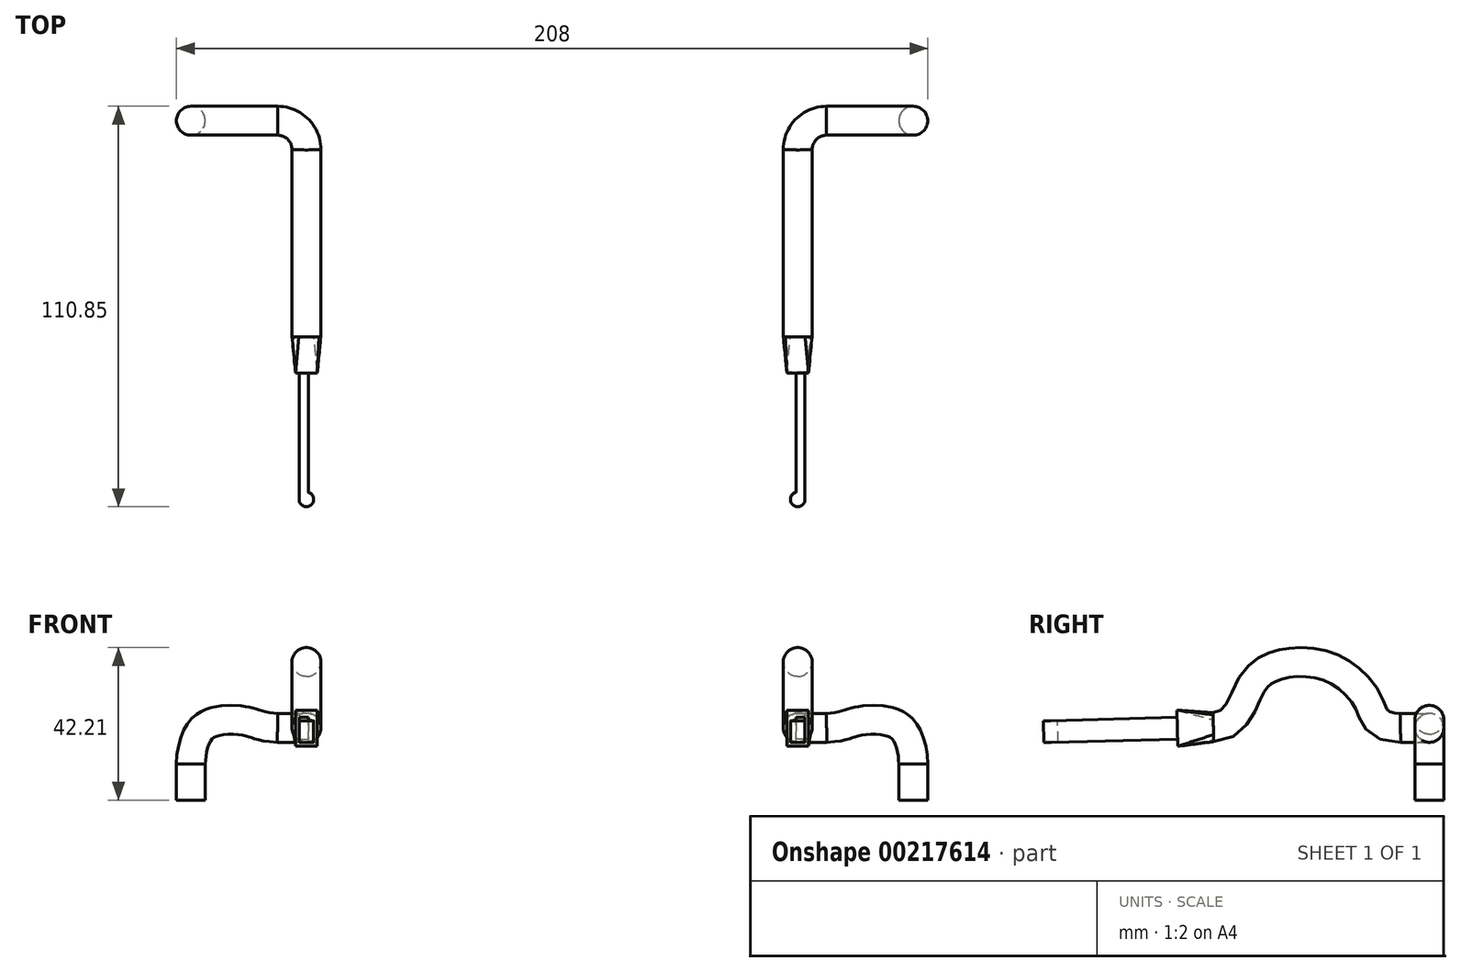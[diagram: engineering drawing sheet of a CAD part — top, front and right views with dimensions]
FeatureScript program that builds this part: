
annotation { "Feature Type Name" : "Feature", "Feature Type Description" : "" }
export const myFeature = defineFeature(function(context is Context, id is Id, definition is map)
    precondition{}
    {
        {
            var Q0;
            Q0=qCreatedBy(makeId("Top.planeOp"),FACE);
            var sketch = newSketch(context, id + "F0", { "sketchPlane" : qUnion([Q0])});
            skCircle(sketch, "E0", {"center": v(0, 0) * mm, "radius": 4 * mm});
            skSolve(sketch);
        }
        {
            var Q0;
            Q0=qCreatedBy(makeId("Front.planeOp"),FACE);
            var sketch = newSketch(context, id + "F1", { "sketchPlane" : qUnion([Q0])});
            skFitSpline(sketch, "E1", {"points": [v(0, 0) * mm, v(3.76, 10.37) * mm, v(16.57, 11.55) * mm, v(24, 10) * mm], "startDerivative": vector(0.87, 24.08) * mm, "endDerivative": vector(51.38, -2.87) * mm});
            skSolve(sketch);
        }
        {
            var Q0;
            Q0=makeQuery(id+"F0.imprint","IMPRINT",FACE,{"disambiguationData":[TD([[makeQuery(id+"F0.imprint","IMPRINT",EDGE,{"derivedFrom":sQuery(id+"F0.wireOp",EDGE,"E0")}),1.0]])]});
            var Q1;
            Q1=sQuery(id+"F1.wireOp",EDGE,"E1");
            sweep(context, id + "F2", {"profiles" : qUnion([Q0]), "path" : qUnion([Q1])});
        }
        {
            var Q0;
            Q0=makeQuery(id+"F2.opSweep","CAP_FACE",FACE,{"disambiguationData":[OSD([sQuery(id+"F0.wireOp",EDGE,"E0"),sQuery(id+"F1.wireOp",VERTEX,"E1.start")])],"isStart":true});
            extrude(context, id + "F3", {"entities" : qUnion([Q0]), "operationType" : NewBodyOperationType.ADD, "depth" : 10 * mm});
        }
        {
            var Q0;
            Q0=makeQuery(id+"F2.opSweep","CAP_FACE",FACE,{"disambiguationData":[OSD([sQuery(id+"F0.wireOp",EDGE,"E0"),sQuery(id+"F1.wireOp",VERTEX,"E1.end")])],"isStart":false});
            var sketch = newSketch(context, id + "F4", { "sketchPlane" : qUnion([Q0])});
            skCircle(sketch, "E2.0", {"center": v(0, 10.47) * mm, "radius": 4 * mm});
            skSolve(sketch);
        }
        {
            var Q0;
            Q0=sQuery(id+"F4.wireOp",VERTEX,"E2.0.center");
            var Q1;
            Q1=qCreatedBy(makeId("Top.planeOp"),FACE);
            cPlane(context, id + "F5", {"entities" : qUnion([Q0, Q1]), "cplaneType" : CPlaneType.PLANE_POINT, "offset" : 25 * mm, "width" : 150 * mm, "height" : 150 * mm});
        }
        {
            var Q0;
            Q0=qCreatedBy(id+"F5.planeOp",FACE);
            var sketch = newSketch(context, id + "F6", { "sketchPlane" : qUnion([Q0])});
            skArc(sketch, "E3", {"start": v(32, -8) * mm, "mid": v(29.66, -2.34) * mm, "end": v(24, 0) * mm});
            skLineSegment(sketch, "E4", {"start": v(24, 0) * mm, "end": v(24, -8) * mm, "construction": true});
            skLineSegment(sketch, "E5", {"start": v(24, -8) * mm, "end": v(24, -16) * mm, "construction": true});
            skLineSegment(sketch, "E6", {"start": v(24, -8) * mm, "end": v(32, -8) * mm, "construction": true});
            skSolve(sketch);
        }
        {
            var Q0;
            Q0=makeQuery(id+"F4.imprint","IMPRINT",FACE,{"disambiguationData":[TD([[makeQuery(id+"F4.imprint","IMPRINT",EDGE,{"derivedFrom":sQuery(id+"F4.wireOp",EDGE,"E2.0")}),1.0]])]});
            var Q1;
            Q1=sQuery(id+"F6.wireOp",EDGE,"E3");
            sweep(context, id + "F7", {"operationType" : NewBodyOperationType.ADD, "profiles" : qUnion([Q0]), "path" : qUnion([Q1])});
        }
        {
            var Q0;
            Q0=makeQuery(id+"F7.opSweep","CAP_FACE",FACE,{"disambiguationData":[OSD([sQuery(id+"F4.wireOp",EDGE,"E2.0"),sQuery(id+"F6.wireOp",VERTEX,"E3.start")])],"isStart":false});
            var sketch = newSketch(context, id + "F8", { "sketchPlane" : qUnion([Q0])});
            skCircle(sketch, "E7.0", {"center": v(32, 10.16) * mm, "radius": 4 * mm});
            skSolve(sketch);
        }
        {
            var Q0;
            Q0=qCreatedBy(makeId("Right.planeOp"),FACE);
            var Q1;
            Q1=sQuery(id+"F8.wireOp",VERTEX,"E7.0.center");
            cPlane(context, id + "F9", {"entities" : qUnion([Q0, Q1]), "cplaneType" : CPlaneType.PLANE_POINT, "offset" : 25 * mm, "width" : 150 * mm, "height" : 150 * mm});
        }
        {
            var Q0;
            Q0=qCreatedBy(id+"F9.planeOp",FACE);
            var sketch = newSketch(context, id + "F10", { "sketchPlane" : qUnion([Q0])});
            skPoint(sketch, "E8.0", {"position": v(0, 25) * mm});
            skFitSpline(sketch, "E9", {"points": [v(-8, 10) * mm, v(-16.65, 16.64) * mm, v(-25.4, 25.82) * mm, v(-36.84, 28.18) * mm, v(-45.16, 26) * mm, v(-50.1, 20.25) * mm, v(-59.78, 10.18) * mm], "startDerivative": vector(-128.08, 0.95) * mm, "endDerivative": vector(-95.04, 0) * mm});
            skSolve(sketch);
        }
        {
            var Q0;
            Q0=makeQuery(id+"F8.imprint","IMPRINT",FACE,{"disambiguationData":[TD([[makeQuery(id+"F8.imprint","IMPRINT",EDGE,{"derivedFrom":sQuery(id+"F8.wireOp",EDGE,"E7.0")}),1.0]])]});
            var Q1;
            Q1 = qConstructionFilter(qBodyType(qCreatedBy(id + "F10" ,EDGE), BodyType.WIRE), ConstructionObject.NO);
            sweep(context, id + "F11", {"operationType" : NewBodyOperationType.ADD, "profiles" : qUnion([Q0]), "path" : qUnion([Q1])});
        }
        {
            var Q0;
            Q0=makeQuery(id+"F11.opSweep","CAP_FACE",FACE,{"disambiguationData":[OSD([sQuery(id+"F4.wireOp",EDGE,"E2.0"),sQuery(id+"F10.wireOp",VERTEX,"E9.end")])],"isStart":false});
            cPlane(context, id + "F12", {"entities" : qUnion([Q0]), "cplaneType" : CPlaneType.OFFSET, "offset" : 10 * mm, "width" : 150 * mm, "height" : 150 * mm});
        }
        {
            var Q0;
            Q0=qCreatedBy(id+"F12.planeOp",FACE);
            var sketch = newSketch(context, id + "F13", { "sketchPlane" : qUnion([Q0])});
            skLineSegment(sketch, "E10.bottom", {"start": v(29, 16.8) * mm, "end": v(35, 16.8) * mm});
            skLineSegment(sketch, "E10.top", {"start": v(29, 6.8) * mm, "end": v(35, 6.8) * mm});
            skLineSegment(sketch, "E10.left", {"start": v(29, 16.8) * mm, "end": v(29, 6.8) * mm});
            skLineSegment(sketch, "E10.right", {"start": v(35, 16.8) * mm, "end": v(35, 6.8) * mm});
            skCircle(sketch, "E11.0", {"center": v(32, 11.8) * mm, "radius": 4 * mm, "construction": true});
            skSolve(sketch);
        }
        {
            var Q0;
            Q0=makeQuery(id+"F11.opSweep","CAP_FACE",FACE,{"disambiguationData":[OSD([sQuery(id+"F4.wireOp",EDGE,"E2.0"),sQuery(id+"F10.wireOp",VERTEX,"E9.end")])],"isStart":false});
            var sketch = newSketch(context, id + "F14", { "sketchPlane" : qUnion([Q0])});
            skCircle(sketch, "E12.0", {"center": v(32, 11.8) * mm, "radius": 4 * mm});
            skSolve(sketch);
        }
        {
            var Q0;
            Q0 = qSketchRegion(id + "F13", true);
            var Q1;
            Q1 = qSketchRegion(id + "F14", true);
            loft(context, id + "F15", {"operationType" : NewBodyOperationType.ADD, "sheetProfilesArray" : [{ "sheetProfileEntities" : qUnion([Q0]) }, { "sheetProfileEntities" : qUnion([Q1]) }]});
        }
        {
            var Q0;
            Q0=makeQuery(id+"F15.opLoft","CAP_FACE",FACE,{"disambiguationData":[OSD([makeQuery(id+"F13.imprint","IMPRINT",FACE,{"disambiguationData":[TD([[makeQuery(id+"F13.imprint","IMPRINT",EDGE,{"derivedFrom":sQuery(id+"F13.wireOp",EDGE,"E10.bottom")}),-1.0]])]})])],"isStart":true});
            var sketch = newSketch(context, id + "F16", { "sketchPlane" : qUnion([Q0])});
            skLineSegment(sketch, "E13.bottom", {"start": v(30, 14.8) * mm, "end": v(32.5, 14.8) * mm});
            skLineSegment(sketch, "E13.top", {"start": v(30, 8.8) * mm, "end": v(32.5, 8.8) * mm});
            skLineSegment(sketch, "E13.left", {"start": v(30, 14.8) * mm, "end": v(30, 8.8) * mm});
            skLineSegment(sketch, "E13.right", {"start": v(32.5, 14.8) * mm, "end": v(32.5, 8.8) * mm});
            skSolve(sketch);
        }
        {
            var Q0;
            Q0=makeQuery(id+"F16.imprint","IMPRINT",FACE,{"disambiguationData":[TD([[makeQuery(id+"F16.imprint","IMPRINT",EDGE,{"derivedFrom":sQuery(id+"F16.wireOp",EDGE,"E13.bottom")}),-1.0]])]});
            extrude(context, id + "F17", {"entities" : qUnion([Q0]), "operationType" : NewBodyOperationType.ADD, "depth" : 35 * mm});
        }
        {
            var Q0;
            Q0=makeQuery(id+"F17.opExtrude","SWEPT_FACE",FACE,{"disambiguationData":[OSD([sQuery(id+"F16.wireOp",EDGE,"E13.bottom")])]});
            var sketch = newSketch(context, id + "F18", { "sketchPlane" : qUnion([Q0])});
            skCircle(sketch, "E14", {"center": v(32, -104.49) * mm, "radius": 2 * mm});
            skSolve(sketch);
        }
        {
            var Q0;
            {var subQ1=sQuery(id+"F16.wireOp",EDGE,"E13.bottom");var subQ2=makeQuery(id+"F17.opExtrude","CAP_EDGE",EDGE,{"disambiguationData":[OSD([subQ1])],"isStart":false});Q0=makeQuery(id+"F18.imprint","IMPRINT",FACE,{"disambiguationData":[TD([[makeQuery(id+"F18.imprint","IMPRINT",EDGE,{"derivedFrom":subQ2}),-1.0]])]});}
            var Q1;
            Q1=makeQuery(id+"F17.opExtrude","SWEPT_FACE",FACE,{"disambiguationData":[OSD([sQuery(id+"F16.wireOp",EDGE,"E13.top")])]});
            extrude(context, id + "F19", {"entities" : qUnion([Q0]), "operationType" : NewBodyOperationType.ADD, "endBound" : BoundingType.UP_TO_SURFACE, "oppositeDirection" : true, "endBoundEntityFace" : qUnion([Q1]), "depth" : 25 * mm});
        }
        {
            var Q0;
            Q0=qCreatedBy(makeId("Right.planeOp"),FACE);
            cPlane(context, id + "F20", {"entities" : qUnion([Q0]), "cplaneType" : CPlaneType.OFFSET, "offset" : 100 * mm, "width" : 150 * mm, "height" : 150 * mm});
        }
        {
            var Q0;
            Q0=makeQuery(id+"F2.opSweep","SWEPT_BODY",BODY,{"disambiguationData":[OSD([sQuery(id+"F0.wireOp",EDGE,"E0"),sQuery(id+"F1.wireOp",EDGE,"E1")])]});
            var Q1;
            Q1=qCreatedBy(id+"F20.planeOp",FACE);
            mirror(context, id + "F21", {"entities" : qUnion([Q0]), "mirrorPlane" : qUnion([Q1])});
        }
    });
